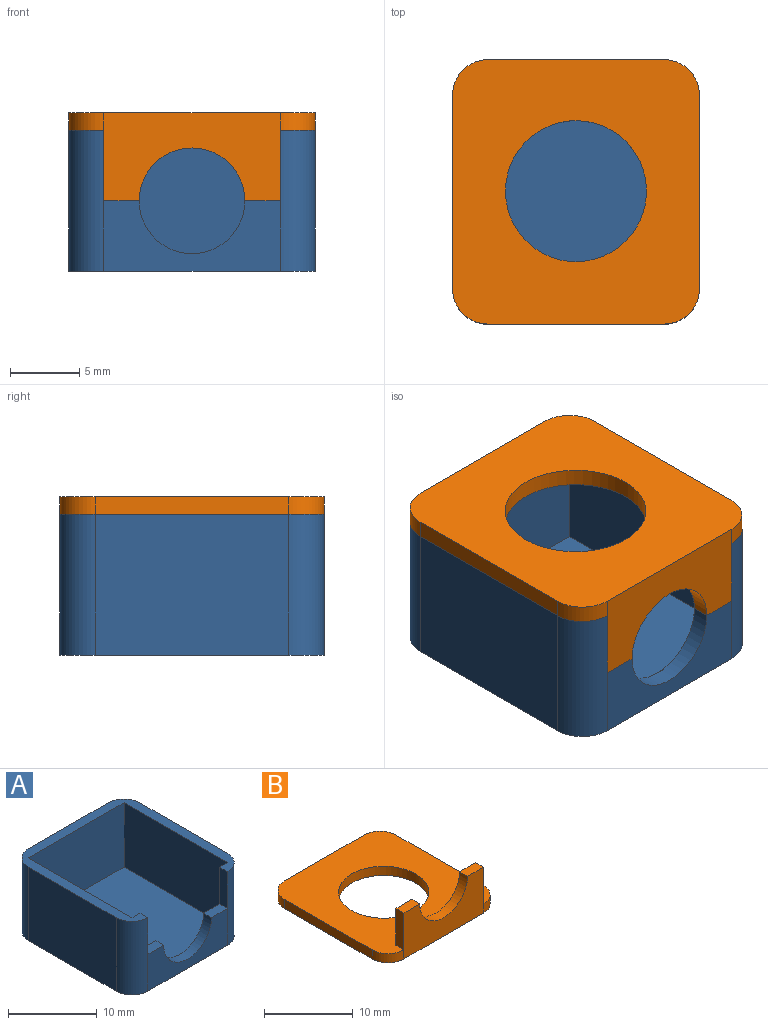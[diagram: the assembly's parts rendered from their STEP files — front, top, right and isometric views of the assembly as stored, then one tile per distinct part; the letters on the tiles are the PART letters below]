
ASSEMBLY  parts=2 mates=1
PART A: 21 faces, bbox 17.8x19.1x10.2 mm
  f0: plane 19.05x17.78mm, normal (0,0,1), area 65.4mm2, adj f1,f2,f3,f5,f7,f8,f9,f10
  f1: plane 8.89x7.62mm, normal (0,1,0), area 24.1mm2, adj f0,f8,f11,f16,f19,f20
  f2: plane 12.7x10.16mm, normal (0,1,0), area 129mm2, adj f0,f6,f12,f15
  f3: plane 13.97x10.16mm, normal (-1,0,0), area 141.9mm2, adj f0,f6,f12,f13
  f4: plane 12.7x5.08mm, normal (0,-1,0), area 41.7mm2, adj f6,f13,f14,f16,f17,f20
  f5: plane 13.97x10.16mm, normal (1,0,0), area 141.9mm2, adj f0,f6,f14,f15
  f6: plane 19.05x17.78mm, normal (0,0,-1), area 333.2mm2, adj f2,f3,f4,f5,f12,f13,f14,f15
  f7: plane 15.24x8.89mm, normal (0,-1,0), area 135.5mm2, adj f0,f8,f10,f11
  f8: plane 16.51x8.89mm, normal (1,0,0), area 146.8mm2, adj f0,f1,f7,f11
  f9: plane 8.89x7.62mm, normal (0,1,0), area 24.1mm2, adj f0,f10,f11,f16,f17,f18
  f10: plane 16.51x8.89mm, normal (-1,0,0), area 146.8mm2, adj f0,f7,f9,f11
  f11: plane 16.51x15.24mm, normal (0,0,1), area 251.6mm2, adj f1,f7,f8,f9,f10
  f12: cylinder r=2.54mm len=10.16mm, axis (0,0,1), area 40.5mm2, adj f0,f2,f3,f6
  f13: cylinder r=2.54mm len=10.16mm, axis (0,0,-1), area 40.5mm2, adj f0,f3,f4,f6,f19
  f14: cylinder r=2.54mm len=10.16mm, axis (0,0,1), area 40.5mm2, adj f0,f4,f5,f6,f18
  f15: cylinder r=2.54mm len=10.16mm, axis (0,0,-1), area 40.5mm2, adj f0,f2,f5,f6
  f16: cylinder r=3.81mm len=7.62mm, axis (0,-1,0), area 15.2mm2, adj f1,f4,f9,f17,f20
  f17: plane 2.54x1.27mm, normal (0,0,1), area 3.2mm2, adj f4,f9,f16,f18
  f18: plane 5.08x1.27mm, normal (-1,0,0), area 6.5mm2, adj f0,f9,f14,f17
  f19: plane 5.08x1.27mm, normal (1,0,0), area 6.5mm2, adj f0,f1,f13,f20
  f20: plane 2.54x1.27mm, normal (0,0,1), area 3.2mm2, adj f1,f4,f16,f19
PART B: 17 faces, bbox 17.8x19.1x6.4 mm
  f0: plane 12.7x6.35mm, normal (0,-1,0), area 57.8mm2, adj f2,f7,f9,f10,f12,f13,f14,f15
  f1: plane 12.7x5.08mm, normal (0,1,0), area 41.7mm2, adj f2,f3,f12,f13,f14,f15
  f2: plane 2.54x1.27mm, normal (0,0,1), area 3.2mm2, adj f0,f1,f12,f15
  f3: plane 19.05x17.78mm, normal (0,0,1), area 236mm2, adj f1,f4,f5,f6,f8,f9,f10,f11
  f4: plane 12.7x1.27mm, normal (0,1,0), area 16.1mm2, adj f3,f7,f8,f11
  f5: plane 13.97x1.27mm, normal (-1,0,0), area 17.7mm2, adj f3,f7,f8,f9
  f6: plane 13.97x1.27mm, normal (1,0,0), area 17.7mm2, adj f3,f7,f10,f11
  f7: plane 19.05x17.78mm, normal (0,0,-1), area 252.1mm2, adj f0,f4,f5,f6,f8,f9,f10,f11
  f8: cylinder r=2.54mm len=2.54mm, axis (0,0,1), area 5.1mm2, adj f3,f4,f5,f7
  f9: cylinder r=2.54mm len=2.54mm, axis (0,0,-1), area 5.1mm2, adj f0,f3,f5,f7
  f10: cylinder r=2.54mm len=2.54mm, axis (0,0,1), area 5.1mm2, adj f0,f3,f6,f7
  f11: cylinder r=2.54mm len=2.54mm, axis (0,0,-1), area 5.1mm2, adj f3,f4,f6,f7
  f12: plane 5.08x1.27mm, normal (-1,0,0), area 6.5mm2, adj f0,f1,f2,f3
  f13: plane 5.08x1.27mm, normal (1,0,0), area 6.5mm2, adj f0,f1,f3,f14
  f14: plane 2.54x1.27mm, normal (0,0,1), area 3.2mm2, adj f0,f1,f13,f15
  f15: cylinder r=3.81mm len=7.62mm, axis (0,-1,0), area 15.2mm2, adj f0,f1,f2,f14
  f16: cylinder r=5.08mm len=10.16mm, axis (0,0,1), area 40.5mm2, adj f3,f7
PLACE A rot(axis=(0,1,0),0deg) t=(-6.91,-0.71,11.5)mm
PLACE B rot(axis=(0,-1,0),180deg) t=(18.69,-0.83,22.93)mm
MATE fastened B.f13 <-> A.f19  axis (-1,0,0) through (-12,-9.77,19.12)mm
